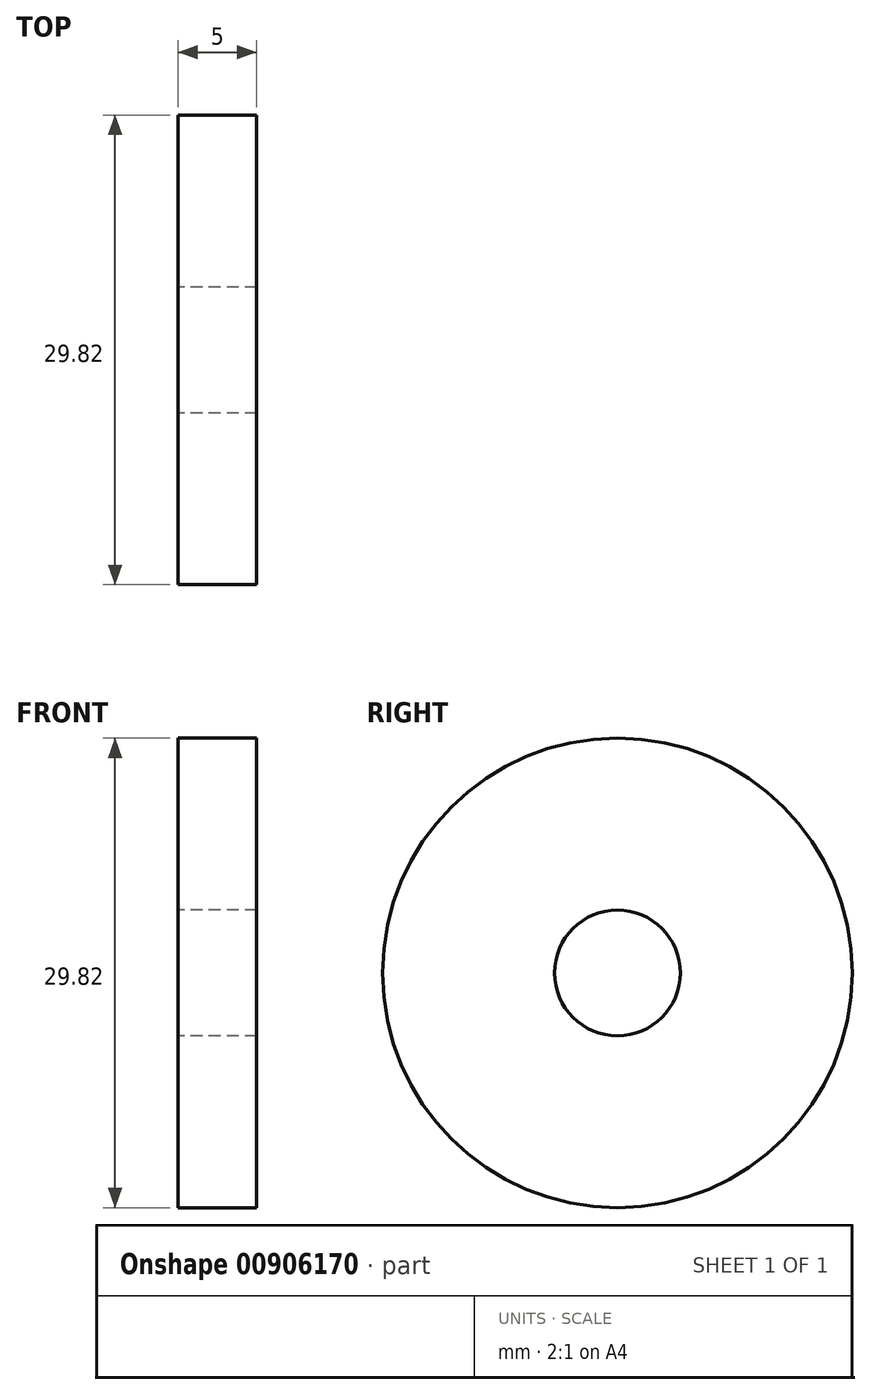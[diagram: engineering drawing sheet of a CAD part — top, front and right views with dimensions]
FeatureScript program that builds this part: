
annotation { "Feature Type Name" : "Feature", "Feature Type Description" : "" }
export const myFeature = defineFeature(function(context is Context, id is Id, definition is map)
    precondition{}
    {
        {
            var Q0;
            Q0=qCreatedBy(makeId("Right.planeOp"),FACE);
            var sketch = newSketch(context, id + "F0", { "sketchPlane" : qUnion([Q0])});
            skCircle(sketch, "E0", {"center": v(0, 0) * mm, "radius": 14.91 * mm});
            skCircle(sketch, "E1", {"center": v(0, 0) * mm, "radius": 4 * mm});
            skSolve(sketch);
        }
        {
            var Q0;
            Q0 = qSketchRegion(id + "F0", true);
            extrude(context, id + "F1", {"entities" : qUnion([Q0]), "depth" : 5 * mm, "offsetDistance" : 25 * mm});
        }
    });
